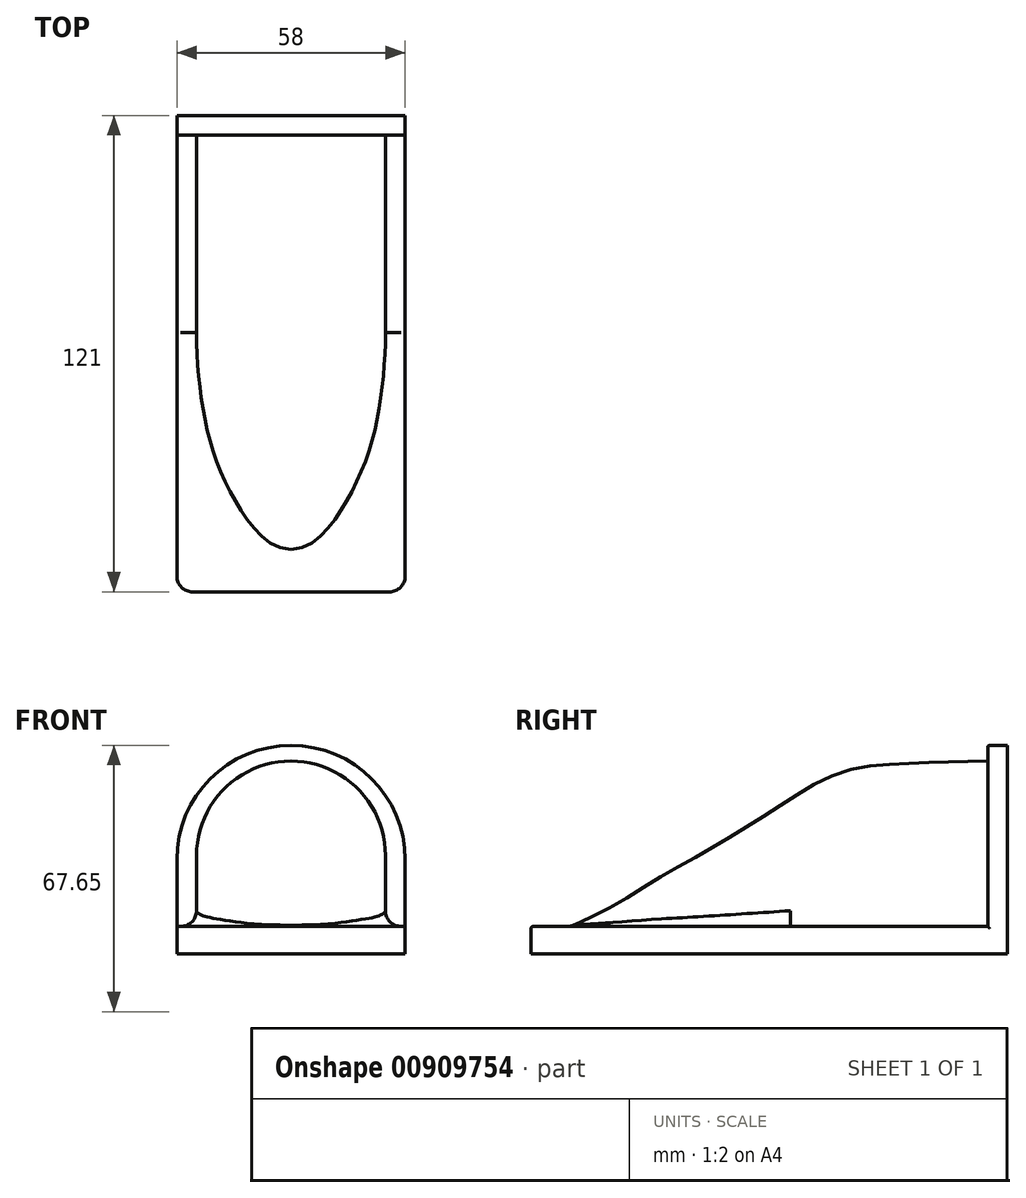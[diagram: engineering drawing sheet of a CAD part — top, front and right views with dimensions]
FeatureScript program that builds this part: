
annotation { "Feature Type Name" : "Feature", "Feature Type Description" : "" }
export const myFeature = defineFeature(function(context is Context, id is Id, definition is map)
    precondition{}
    {
        {
            var Q0;
            Q0=qCreatedBy(makeId("Top.planeOp"),FACE);
            var sketch = newSketch(context, id + "F0", { "sketchPlane" : qUnion([Q0])});
            skLineSegment(sketch, "E0.bottom", {"start": v(29, 60.5) * mm, "end": v(-29, 60.5) * mm});
            skLineSegment(sketch, "E0.top", {"start": v(29, -60.5) * mm, "end": v(-29, -60.5) * mm});
            skLineSegment(sketch, "E0.left", {"start": v(29, 60.5) * mm, "end": v(29, -60.5) * mm});
            skLineSegment(sketch, "E0.right", {"start": v(-29, 60.5) * mm, "end": v(-29, -60.5) * mm});
            skPoint(sketch, "E0.middle", {"position": v(0, 0) * mm});
            skSolve(sketch);
        }
        {
            var Q0;
            Q0 = qSketchRegion(id + "F0", true);
            extrude(context, id + "F1", {"entities" : qUnion([Q0]), "depth" : 7 * mm, "offsetDistance" : 25 * mm});
        }
        {
            var Q0;
            Q0=qCreatedBy(makeId("Right.planeOp"),FACE);
            var sketch = newSketch(context, id + "F2", { "sketchPlane" : qUnion([Q0])});
            skLineSegment(sketch, "E1.bottom", {"start": v(55.5, 7) * mm, "end": v(-55.5, 7) * mm});
            skLineSegment(sketch, "E1.top", {"start": v(55.5, -7) * mm, "end": v(-55.5, -7) * mm});
            skLineSegment(sketch, "E1.left", {"start": v(55.5, 7) * mm, "end": v(55.5, -7) * mm});
            skLineSegment(sketch, "E1.right", {"start": v(-55.5, 7) * mm, "end": v(-55.5, -7) * mm});
            skPoint(sketch, "E1.middle", {"position": v(0, 0) * mm});
            skLineSegment(sketch, "E2", {"start": v(-55.5, 7) * mm, "end": v(-50.5, 7) * mm});
            skLineSegment(sketch, "E3", {"start": v(55.5, 7) * mm, "end": v(55.5, 53) * mm});
            skLineSegment(sketch, "E4", {"start": v(55.5, 53) * mm, "end": v(55.5, 49) * mm});
            skFitSpline(sketch, "E5", {"points": [v(-50.5, 7) * mm, v(-39.35, 12.33) * mm, v(-28.76, 18.88) * mm, v(-18.4, 24.78) * mm, v(-7.15, 31.43) * mm, v(2.35, 37.44) * mm, v(11.95, 43.33) * mm, v(22.43, 47.26) * mm, v(34, 48.35) * mm, v(55.5, 49) * mm], "startDerivative": vector(132.05, 57.7) * mm, "endDerivative": vector(186.13, 0.14) * mm});
            skLineSegment(sketch, "E6.bottom", {"start": v(55.5, 0) * mm, "end": v(60.5, 0) * mm});
            skLineSegment(sketch, "E6.top", {"start": v(55.5, 49) * mm, "end": v(60.5, 49) * mm});
            skLineSegment(sketch, "E6.left", {"start": v(55.5, 0) * mm, "end": v(55.5, 49) * mm});
            skLineSegment(sketch, "E6.right", {"start": v(60.5, 0) * mm, "end": v(60.5, 49) * mm});
            skLineSegment(sketch, "E7", {"start": v(55.5, 53) * mm, "end": v(60.5, 53) * mm});
            skLineSegment(sketch, "E8", {"start": v(60.5, 53) * mm, "end": v(60.5, 49) * mm});
            skSolve(sketch);
        }
        {
            var Q0;
            {var subQ3=sQuery(id+"F2.wireOp",EDGE,"E5");Q0=makeQuery(id+"F2.imprint","IMPRINT",FACE,{"disambiguationData":[TD([[makeQuery(id+"F2.imprint","IMPRINT",EDGE,{"derivedFrom":subQ3}),-1.0]])]});}
            extrude(context, id + "F3", {"entities" : qUnion([Q0]), "operationType" : NewBodyOperationType.ADD, "depth" : 24 * mm, "offsetDistance" : 25 * mm, "hasSecondDirection" : true, "secondDirectionOppositeDirection" : true, "secondDirectionDepth" : 24 * mm});
        }
        {
            var Q0;
            Q0=makeQuery(id+"F3.opExtrude","CAP_EDGE",EDGE,{"disambiguationData":[OSD([sQuery(id+"F2.wireOp",EDGE,"E5")])],"isStart":true});
            var Q1;
            Q1=makeQuery(id+"F3.opExtrude","CAP_EDGE",EDGE,{"disambiguationData":[OSD([sQuery(id+"F2.wireOp",EDGE,"E5")])],"isStart":false});
            fillet(context, id + "F4", {"entities" : qUnion([Q0, Q1]), "radius" : 24 * mm, "tangentPropagation" : true, "allowEdgeOverflow" : false});
        }
        {
            var Q0;
            Q0=makeQuery(id+"F4.opFillet","BLEND_EDGE",EDGE,{"blendedFrom":[makeQuery(id+"F3.opExtrude","CAP_EDGE",EDGE,{"disambiguationData":[OSD([sQuery(id+"F2.wireOp",EDGE,"E5")])],"isStart":false}),makeQuery(id+"F1.opExtrude","CAP_FACE",FACE,{"disambiguationData":[OSD([sQuery(id+"F0.wireOp",EDGE,"E0.bottom"),sQuery(id+"F0.wireOp",EDGE,"E0.top"),sQuery(id+"F0.wireOp",EDGE,"E0.left"),sQuery(id+"F0.wireOp",EDGE,"E0.right")])],"isStart":false})],"blendedInto":[makeQuery(id+"F1.opExtrude","CAP_FACE",FACE,{"disambiguationData":[OSD([sQuery(id+"F0.wireOp",EDGE,"E0.bottom"),sQuery(id+"F0.wireOp",EDGE,"E0.top"),sQuery(id+"F0.wireOp",EDGE,"E0.left"),sQuery(id+"F0.wireOp",EDGE,"E0.right")])],"isStart":false})]});
            var Q1;
            Q1=makeQuery(id+"F4.opFillet","BLEND_EDGE",EDGE,{"blendedFrom":[makeQuery(id+"F3.opExtrude","CAP_EDGE",EDGE,{"disambiguationData":[OSD([sQuery(id+"F2.wireOp",EDGE,"E5")])],"isStart":true}),makeQuery(id+"F1.opExtrude","CAP_FACE",FACE,{"disambiguationData":[OSD([sQuery(id+"F0.wireOp",EDGE,"E0.bottom"),sQuery(id+"F0.wireOp",EDGE,"E0.top"),sQuery(id+"F0.wireOp",EDGE,"E0.left"),sQuery(id+"F0.wireOp",EDGE,"E0.right")])],"isStart":false})],"blendedInto":[makeQuery(id+"F1.opExtrude","CAP_FACE",FACE,{"disambiguationData":[OSD([sQuery(id+"F0.wireOp",EDGE,"E0.bottom"),sQuery(id+"F0.wireOp",EDGE,"E0.top"),sQuery(id+"F0.wireOp",EDGE,"E0.left"),sQuery(id+"F0.wireOp",EDGE,"E0.right")])],"isStart":false})]});
            var Q2;
            Q2=makeQuery(id+"F3.opExtrude","CAP_EDGE",EDGE,{"disambiguationData":[OSD([sQuery(id+"F2.wireOp",EDGE,"E1.bottom")])],"isStart":false});
            var Q3;
            Q3=makeQuery(id+"F3.opExtrude","CAP_EDGE",EDGE,{"disambiguationData":[OSD([sQuery(id+"F2.wireOp",EDGE,"E1.bottom")])],"isStart":true});
            fillet(context, id + "F5", {"entities" : qUnion([Q0, Q1, Q2, Q3]), "radius" : 4 * mm, "tangentPropagation" : true, "allowEdgeOverflow" : false});
        }
        {
            var Q0;
            {var subQ4=sQuery(id+"F2.wireOp",EDGE,"E6.bottom");Q0=makeQuery(id+"F2.imprint","IMPRINT",FACE,{"disambiguationData":[TD([[makeQuery(id+"F2.imprint","IMPRINT",EDGE,{"derivedFrom":subQ4}),1.0]])]});}
            var Q1;
            {var subQ2=sQuery(id+"F2.wireOp",EDGE,"E6.top");Q1=makeQuery(id+"F2.imprint","IMPRINT",FACE,{"disambiguationData":[TD([[makeQuery(id+"F2.imprint","IMPRINT",EDGE,{"derivedFrom":subQ2}),1.0]])]});}
            extrude(context, id + "F6", {"entities" : qUnion([Q0, Q1]), "operationType" : NewBodyOperationType.ADD, "depth" : 29 * mm, "offsetDistance" : 25 * mm, "hasSecondDirection" : true, "secondDirectionOppositeDirection" : true, "secondDirectionDepth" : 29 * mm});
        }
        {
            var Q0;
            Q0=makeQuery(id+"F6.opExtrude","CAP_EDGE",EDGE,{"disambiguationData":[OSD([sQuery(id+"F2.wireOp",EDGE,"E7")])],"isStart":false});
            var Q1;
            Q1=makeQuery(id+"F6.opExtrude","CAP_EDGE",EDGE,{"disambiguationData":[OSD([sQuery(id+"F2.wireOp",EDGE,"E7")])],"isStart":true});
            fillet(context, id + "F7", {"entities" : qUnion([Q0, Q1]), "radius" : 29 * mm, "tangentPropagation" : true, "allowEdgeOverflow" : false});
        }
        {
            var Q0;
            Q0=makeQuery(id+"F6.opExtrude","CAP_EDGE",EDGE,{"disambiguationData":[OSD([sQuery(id+"F2.wireOp",EDGE,"E1.left"),sQuery(id+"F2.wireOp",EDGE,"E3")])],"isStart":false});
            var Q1;
            Q1=makeQuery(id+"F1.opExtrude","CAP_EDGE",EDGE,{"disambiguationData":[OSD([sQuery(id+"F0.wireOp",EDGE,"E0.left")])],"isStart":false});
            var Q2;
            Q2=makeQuery(id+"F1.opExtrude","CAP_EDGE",EDGE,{"disambiguationData":[OSD([sQuery(id+"F0.wireOp",EDGE,"E0.top")])],"isStart":false});
            var Q3;
            Q3=makeQuery(id+"F1.opExtrude","CAP_EDGE",EDGE,{"disambiguationData":[OSD([sQuery(id+"F0.wireOp",EDGE,"E0.right")])],"isStart":false});
            var Q4;
            Q4=makeQuery(id+"F6.opExtrude","CAP_EDGE",EDGE,{"disambiguationData":[OSD([sQuery(id+"F2.wireOp",EDGE,"E1.left"),sQuery(id+"F2.wireOp",EDGE,"E3")])],"isStart":true});
            var Q5;
            Q5=makeQuery(id+"F7.opFillet","BLEND_EDGE",EDGE,{"blendedFrom":[makeQuery(id+"F6.opExtrude","CAP_EDGE",EDGE,{"disambiguationData":[OSD([sQuery(id+"F2.wireOp",EDGE,"E7")])],"isStart":true}),makeQuery(id+"F6.opExtrude","SWEPT_FACE",FACE,{"disambiguationData":[OSD([sQuery(id+"F2.wireOp",EDGE,"E1.left"),sQuery(id+"F2.wireOp",EDGE,"E3")])]})],"blendedInto":[makeQuery(id+"F6.opExtrude","SWEPT_FACE",FACE,{"disambiguationData":[OSD([sQuery(id+"F2.wireOp",EDGE,"E1.left"),sQuery(id+"F2.wireOp",EDGE,"E3")])]})]});
            var Q6;
            Q6=makeQuery(id+"F4.opFillet","BLEND_EDGE",EDGE,{"blendedFrom":[makeQuery(id+"F3.opExtrude","CAP_EDGE",EDGE,{"disambiguationData":[OSD([sQuery(id+"F2.wireOp",EDGE,"E5")])],"isStart":false}),makeQuery(id+"F3.opExtrude","SWEPT_FACE",FACE,{"disambiguationData":[OSD([sQuery(id+"F2.wireOp",EDGE,"E3")])]})],"blendedInto":[makeQuery(id+"F3.opExtrude","SWEPT_FACE",FACE,{"disambiguationData":[OSD([sQuery(id+"F2.wireOp",EDGE,"E3")])]})]});
            fillet(context, id + "F8", {"entities" : qUnion([Q0, Q1, Q2, Q3, Q4, Q5, Q6]), "radius" : 0.5 * mm, "allowEdgeOverflow" : false});
        }
        {
            var Q0;
            Q0=makeQuery(id+"F1.opExtrude","SWEPT_EDGE",EDGE,{"disambiguationData":[OSD([sQuery(id+"F0.wireOp",EDGE,"E0.top"),sQuery(id+"F0.wireOp",EDGE,"E0.right")])]});
            var Q1;
            Q1=makeQuery(id+"F1.opExtrude","SWEPT_EDGE",EDGE,{"disambiguationData":[OSD([sQuery(id+"F0.wireOp",EDGE,"E0.top"),sQuery(id+"F0.wireOp",EDGE,"E0.left")])]});
            fillet(context, id + "F9", {"entities" : qUnion([Q0, Q1]), "radius" : 4 * mm, "tangentPropagation" : true, "allowEdgeOverflow" : false});
        }
    });
